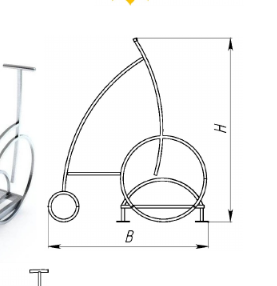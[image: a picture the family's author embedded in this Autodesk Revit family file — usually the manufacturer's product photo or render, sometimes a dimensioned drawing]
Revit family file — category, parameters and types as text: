
# Revit family: 7273 Велопарковка VELO-3 Хоббика
name_source: partatom
category: Антураж
revit_build: Autodesk Revit 2018 (Build: 20180423_1000(x64)
units: mm (PartAtom-declared; Revit-internal decimal feet)

## family parameters
Всегда вертикально = Да
Источник визуального образа = Геометрия семейства
На основе рабочей плоскости = Нет
Общий = Нет
При загрузке вырезать с полостями = Нет
Точка расчета площади = Нет

## types (2) — shared parameters
URL = https://hobbyka.ru
Артикул товара = Арт. 7273
Высота = 268 мм
Группа модели = Велопарковки
Изготовитель = ООО «Хоббика
Материал изделия = Сталь
Цвет каркаса = Сталь
Ширина = 600 мм

## per-type parameters (varying)
| type | Версия на 4 места | Версия на 7 мест | Длина | Изображение типоразмера | Кол-во мест | Описание |
| Версия на 4 места | Да | Нет | 1400 мм | Велопарковка VELO-3 Арт 7273 4 места.jpg | 4 | Велопарковка VELO-3. Версия на 4 места |
| Версия на 7 мест | Нет | Да | 2620 мм | Велопарковка VELO-3 Арт 7273 7 мест.jpg | 7 | Велопарковка VELO-3. Версия на 7 мест |
